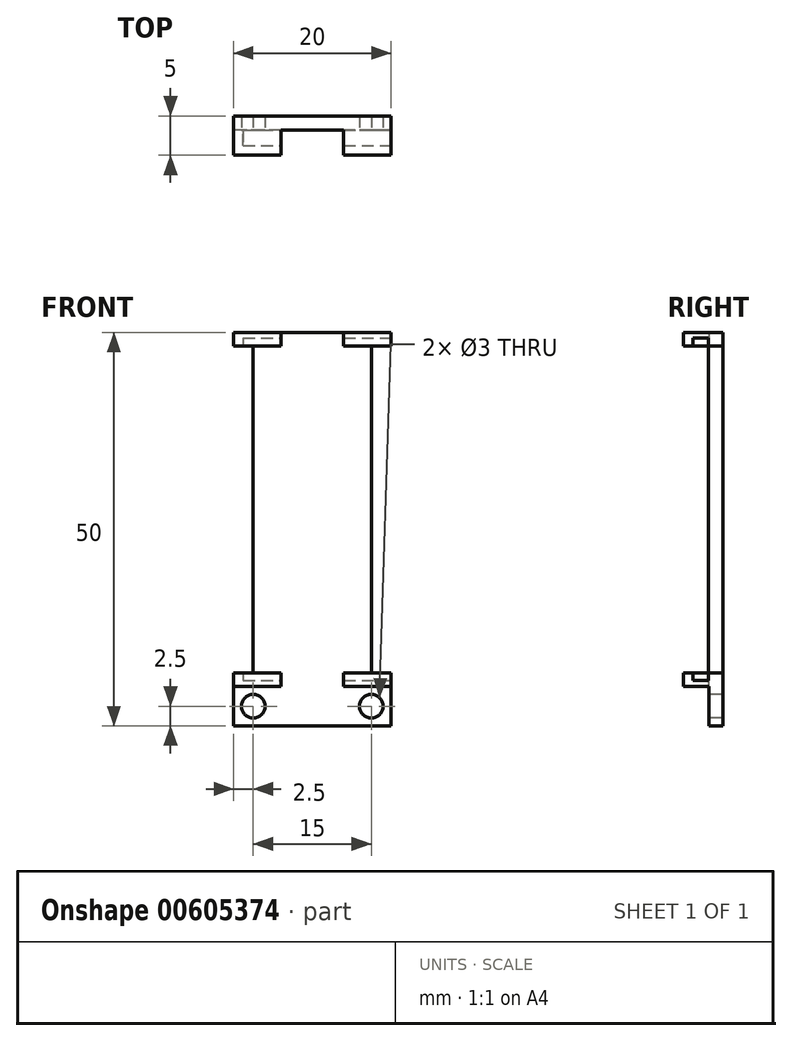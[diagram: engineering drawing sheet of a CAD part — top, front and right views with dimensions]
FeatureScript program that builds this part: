
annotation { "Feature Type Name" : "Feature", "Feature Type Description" : "" }
export const myFeature = defineFeature(function(context is Context, id is Id, definition is map)
    precondition{}
    {
        {
            var Q0;
            Q0=qCreatedBy(makeId("Front.planeOp"),FACE);
            var sketch = newSketch(context, id + "F0", { "sketchPlane" : qUnion([Q0])});
            skLineSegment(sketch, "E0.bottom", {"start": v(10, 22.5) * mm, "end": v(-10, 22.5) * mm});
            skLineSegment(sketch, "E0.top", {"start": v(10, -22.5) * mm, "end": v(-10, -22.5) * mm});
            skLineSegment(sketch, "E0.left", {"start": v(10, 22.5) * mm, "end": v(10, -22.5) * mm});
            skLineSegment(sketch, "E0.right", {"start": v(-10, 22.5) * mm, "end": v(-10, -22.5) * mm});
            skPoint(sketch, "E0.middle", {"position": v(0, 0) * mm});
            skSolve(sketch);
        }
        {
            var Q0;
            Q0=qSketchRegion(id+"F0",true);
            extrude(context, id + "F1", {"entities" : qUnion([Q0]), "depth" : 5 * mm, "offsetDistance" : 25 * mm});
        }
        {
            var Q0;
            Q0=makeQuery(id+"F1.opExtrude","SWEPT_FACE",FACE,{"disambiguationData":[OSD([sQuery(id+"F0.wireOp",EDGE,"E0.left")])]});
            var sketch = newSketch(context, id + "F2", { "sketchPlane" : qUnion([Q0])});
            skLineSegment(sketch, "E1.bottom", {"start": v(-3.8, 21.75) * mm, "end": v(-1.8, 21.75) * mm});
            skLineSegment(sketch, "E1.top", {"start": v(-3.8, -21.75) * mm, "end": v(-1.8, -21.75) * mm});
            skLineSegment(sketch, "E1.left", {"start": v(-3.8, 21.75) * mm, "end": v(-3.8, -21.75) * mm});
            skLineSegment(sketch, "E1.right", {"start": v(-1.8, 21.75) * mm, "end": v(-1.8, -21.75) * mm});
            skPoint(sketch, "E1.middle", {"position": v(-2.8, 0) * mm});
            skSolve(sketch);
        }
        {
            var Q0;
            Q0=qSketchRegion(id+"F2",true);
            extrude(context, id + "F3", {"entities" : qUnion([Q0]), "operationType" : NewBodyOperationType.REMOVE, "oppositeDirection" : true, "depth" : 18.8 * mm, "offsetDistance" : 25 * mm});
        }
        {
            var Q0;
            Q0=makeQuery(id+"F1.opExtrude","SWEPT_FACE",FACE,{"disambiguationData":[OSD([sQuery(id+"F0.wireOp",EDGE,"E0.left")])]});
            var sketch = newSketch(context, id + "F4", { "sketchPlane" : qUnion([Q0])});
            skLineSegment(sketch, "E2.bottom", {"start": v(-3.8, -20.75) * mm, "end": v(-5.05, -20.75) * mm});
            skLineSegment(sketch, "E2.top", {"start": v(-3.8, 20.75) * mm, "end": v(-5.05, 20.75) * mm});
            skLineSegment(sketch, "E2.left", {"start": v(-3.8, -20.75) * mm, "end": v(-3.8, 20.75) * mm});
            skLineSegment(sketch, "E2.right", {"start": v(-5.05, -20.75) * mm, "end": v(-5.05, 20.75) * mm});
            skPoint(sketch, "E2.middle", {"position": v(-4.43, 0) * mm});
            skPoint(sketch, "E2.middle.positionSnap0", {"position": v(-5, 0) * mm});
            skPoint(sketch, "E2.centerSnap0", {"position": v(-5, 0) * mm});
            skSolve(sketch);
        }
        {
            var Q0;
            Q0=qSketchRegion(id+"F4",true);
            extrude(context, id + "F5", {"entities" : qUnion([Q0]), "operationType" : NewBodyOperationType.REMOVE, "oppositeDirection" : true, "depth" : 18.8 * mm, "offsetDistance" : 25 * mm});
        }
        {
            var Q0;
            Q0=makeQuery(id+"F1.opExtrude","CAP_FACE",FACE,{"disambiguationData":[OSD([sQuery(id+"F0.wireOp",EDGE,"E0.bottom"),sQuery(id+"F0.wireOp",EDGE,"E0.top"),sQuery(id+"F0.wireOp",EDGE,"E0.left"),sQuery(id+"F0.wireOp",EDGE,"E0.right")])],"isStart":false});
            var sketch = newSketch(context, id + "F6", { "sketchPlane" : qUnion([Q0])});
            skLineSegment(sketch, "E3.bottom", {"start": v(4, 22.95) * mm, "end": v(-4, 22.95) * mm});
            skLineSegment(sketch, "E3.top", {"start": v(4, 18.55) * mm, "end": v(-4, 18.55) * mm});
            skLineSegment(sketch, "E3.left", {"start": v(4, 22.95) * mm, "end": v(4, 18.55) * mm});
            skLineSegment(sketch, "E3.right", {"start": v(-4, 22.95) * mm, "end": v(-4, 18.55) * mm});
            skPoint(sketch, "E3.middle", {"position": v(0, 20.75) * mm});
            skPoint(sketch, "E3.middle.positionSnap0", {"position": v(0, 22.5) * mm});
            skPoint(sketch, "E3.centerSnap0", {"position": v(0, 22.5) * mm});
            skSolve(sketch);
        }
        {
            var Q0;
            Q0=qSketchRegion(id+"F6",true);
            extrude(context, id + "F7", {"entities" : qUnion([Q0]), "operationType" : NewBodyOperationType.REMOVE, "oppositeDirection" : true, "depth" : 3.2 * mm, "offsetDistance" : 25 * mm});
        }
        {
            var Q0;
            {var subQ0=sQuery(id+"F0.wireOp",EDGE,"E0.left");var subQ1=sQuery(id+"F0.wireOp",EDGE,"E0.top");var subQ2=sQuery(id+"F0.wireOp",EDGE,"E0.right");var subQ3=sQuery(id+"F0.wireOp",EDGE,"E0.bottom");Q0=makeQuery(id+"F7.boolean.opBoolean","SPLIT",FACE,{"disambiguationData":[TD([makeQuery(id+"F1.opExtrude","SWEPT_FACE",FACE,{"disambiguationData":[OSD([subQ1])]})])],"derivedFrom":makeQuery(id+"F1.opExtrude","CAP_FACE",FACE,{"disambiguationData":[OSD([subQ3,subQ1,subQ0,subQ2])],"isStart":false})});}
            var sketch = newSketch(context, id + "F8", { "sketchPlane" : qUnion([Q0])});
            skLineSegment(sketch, "E4.bottom", {"start": v(-8.47, -20.75) * mm, "end": v(-10, -20.75) * mm});
            skLineSegment(sketch, "E4.top", {"start": v(-8.47, -19.75) * mm, "end": v(-10, -19.75) * mm});
            skLineSegment(sketch, "E4.left", {"start": v(-8.47, -20.75) * mm, "end": v(-8.47, -19.75) * mm});
            skLineSegment(sketch, "E4.right", {"start": v(-10, -20.75) * mm, "end": v(-10, -19.75) * mm});
            skPoint(sketch, "E4.middle", {"position": v(-9.24, -20.25) * mm});
            skSolve(sketch);
        }
        {
            var Q0;
            Q0=qSketchRegion(id+"F8",true);
            extrude(context, id + "F9", {"entities" : qUnion([Q0]), "operationType" : NewBodyOperationType.REMOVE, "oppositeDirection" : true, "depth" : 3.19 * mm, "offsetDistance" : 25 * mm});
        }
        {
            var Q0;
            {var subQ0=sQuery(id+"F0.wireOp",EDGE,"E0.right");var subQ4=sQuery(id+"F0.wireOp",EDGE,"E0.left");var subQ6=sQuery(id+"F0.wireOp",EDGE,"E0.top");var subQ7=makeQuery(id+"F1.opExtrude","SWEPT_FACE",FACE,{"disambiguationData":[OSD([subQ6])]});var subQ8=sQuery(id+"F0.wireOp",EDGE,"E0.bottom");Q0=makeQuery(id+"F9.boolean.opBoolean","SPLIT",FACE,{"disambiguationData":[TD([subQ7])],"derivedFrom":makeQuery(id+"F7.boolean.opBoolean","SPLIT",FACE,{"disambiguationData":[TD([subQ7])],"derivedFrom":makeQuery(id+"F1.opExtrude","CAP_FACE",FACE,{"disambiguationData":[OSD([subQ8,subQ6,subQ4,subQ0])],"isStart":false})})});}
            var sketch = newSketch(context, id + "F10", { "sketchPlane" : qUnion([Q0])});
            skLineSegment(sketch, "E5.bottom", {"start": v(4, -24.52) * mm, "end": v(-4, -24.52) * mm});
            skLineSegment(sketch, "E5.top", {"start": v(4, -20.75) * mm, "end": v(-4, -20.75) * mm});
            skLineSegment(sketch, "E5.left", {"start": v(4, -24.52) * mm, "end": v(4, -20.75) * mm});
            skLineSegment(sketch, "E5.right", {"start": v(-4, -24.52) * mm, "end": v(-4, -20.75) * mm});
            skPoint(sketch, "E5.middle", {"position": v(0, -22.63) * mm});
            skSolve(sketch);
        }
        {
            var Q0;
            Q0=qSketchRegion(id+"F10",true);
            extrude(context, id + "F11", {"entities" : qUnion([Q0]), "operationType" : NewBodyOperationType.REMOVE, "oppositeDirection" : true, "depth" : 3.2 * mm, "offsetDistance" : 25 * mm});
        }
        {
            var Q0;
            Q0=makeQuery(id+"F3.boolean.opBoolean","COPY",FACE,{"derivedFrom":makeQuery(id+"F3.opExtrude","SWEPT_FACE",FACE,{"disambiguationData":[OSD([sQuery(id+"F2.wireOp",EDGE,"E1.right")])]})});
            var sketch = newSketch(context, id + "F12", { "sketchPlane" : qUnion([Q0])});
            skLineSegment(sketch, "E6.bottom", {"start": v(7.5, 20.75) * mm, "end": v(10, 20.75) * mm});
            skLineSegment(sketch, "E6.top", {"start": v(7.5, -20.75) * mm, "end": v(10, -20.75) * mm});
            skLineSegment(sketch, "E6.left", {"start": v(7.5, 20.75) * mm, "end": v(7.5, -20.75) * mm});
            skLineSegment(sketch, "E6.right", {"start": v(10, 20.75) * mm, "end": v(10, -20.75) * mm});
            skPoint(sketch, "E6.middle", {"position": v(8.75, 0) * mm});
            skLineSegment(sketch, "E7.bottom", {"start": v(-10, 20.75) * mm, "end": v(-7.5, 20.75) * mm});
            skLineSegment(sketch, "E7.top", {"start": v(-10, -20.75) * mm, "end": v(-7.5, -20.75) * mm});
            skLineSegment(sketch, "E7.left", {"start": v(-10, 20.75) * mm, "end": v(-10, -20.75) * mm});
            skLineSegment(sketch, "E7.right", {"start": v(-7.5, 20.75) * mm, "end": v(-7.5, -20.75) * mm});
            skPoint(sketch, "E7.middle", {"position": v(-8.75, 0) * mm});
            skSolve(sketch);
        }
        {
            var Q0;
            Q0=qSketchRegion(id+"F12",true);
            extrude(context, id + "F13", {"entities" : qUnion([Q0]), "operationType" : NewBodyOperationType.REMOVE, "oppositeDirection" : true, "depth" : 25 * mm, "offsetDistance" : 25 * mm, "hasSecondDirection" : true, "secondDirectionOppositeDirection" : false, "secondDirectionDepth" : 25 * mm});
        }
        {
            var Q0;
            Q0=makeQuery(id+"F1.opExtrude","SWEPT_FACE",FACE,{"disambiguationData":[OSD([sQuery(id+"F0.wireOp",EDGE,"E0.top")])]});
            var sketch = newSketch(context, id + "F14", { "sketchPlane" : qUnion([Q0])});
            skLineSegment(sketch, "E8.bottom", {"start": v(10, 0) * mm, "end": v(-10, 0) * mm});
            skLineSegment(sketch, "E8.top", {"start": v(10, 1.8) * mm, "end": v(-10, 1.8) * mm});
            skLineSegment(sketch, "E8.left", {"start": v(10, 0) * mm, "end": v(10, 1.8) * mm});
            skLineSegment(sketch, "E8.right", {"start": v(-10, 0) * mm, "end": v(-10, 1.8) * mm});
            skPoint(sketch, "E8.middle", {"position": v(0, 0.9) * mm});
            skSolve(sketch);
        }
        {
            var Q0;
            Q0=qSketchRegion(id+"F14",true);
            extrude(context, id + "F15", {"entities" : qUnion([Q0]), "operationType" : NewBodyOperationType.ADD, "depth" : 5 * mm, "offsetDistance" : 25 * mm});
        }
        {
            var Q0;
            Q0=makeQuery(id+"F15.boolean.opBoolean","MERGE",FACE,{"derivedFrom":[makeQuery(id+"F11.boolean.opBoolean","COPY",FACE,{"derivedFrom":makeQuery(id+"F11.opExtrude","CAP_FACE",FACE,{"disambiguationData":[OSD([sQuery(id+"F10.wireOp",EDGE,"E5.bottom"),sQuery(id+"F10.wireOp",EDGE,"E5.top"),sQuery(id+"F10.wireOp",EDGE,"E5.left"),sQuery(id+"F10.wireOp",EDGE,"E5.right")])],"isStart":false})}),makeQuery(id+"F15.opExtrude","SWEPT_FACE",FACE,{"disambiguationData":[OSD([sQuery(id+"F14.wireOp",EDGE,"E8.top")])]})]});
            var sketch = newSketch(context, id + "F16", { "sketchPlane" : qUnion([Q0])});
            skCircle(sketch, "E9", {"center": v(-7.5, -25) * mm, "radius": 1.5 * mm});
            skCircle(sketch, "E10", {"center": v(7.5, -25) * mm, "radius": 1.5 * mm});
            skSolve(sketch);
        }
        {
            var Q0;
            Q0=qSketchRegion(id+"F16",true);
            extrude(context, id + "F17", {"entities" : qUnion([Q0]), "operationType" : NewBodyOperationType.REMOVE, "oppositeDirection" : true, "depth" : 25 * mm, "offsetDistance" : 25 * mm});
        }
    });
